# Revit family: Open Fronted Modular Storage With Wooden Door Options
name_source: partatom
category: Furniture
units: mm (PartAtom-declared; Revit-internal decimal feet)

## family parameters
Always vertical = Yes
Cut with Voids When Loaded = No
OmniClass Number = 23.40.20.00
OmniClass Title = General Furniture and Specialties
Room Calculation Point = No
Shared = No
Work Plane-Based = No

## types (1)
- BOF18Z
    BOF10Z Shelves = Yes
    BOF14Z Shelves = Yes
    BOF18Z Shelves = Yes
    Carcass = Gresham - ELM
    Default Elevation = 0 mm  [stored 0 ft]
    Depth = 400 mm  [stored 1.31234 ft]
    Doors = Gresham - PLUM
    Height = 1816 mm  [stored 5.95801 ft]
    Manufacturer = Gresham Office Furniture
    Model = BOOKCASE
    Product Code = BOF18Z
    Range = STORAGE
    Shelves = Gresham - ELM
    URL = www.gof.co.uk
    Width = 1200 mm

note: [stored X ft] marks values corroborated as IEEE doubles in the binary element streams (Revit-internal decimal feet)

## geometry (parser evidence)
native form markers: Sweep x79
no freeform markers — native parametric forms only
